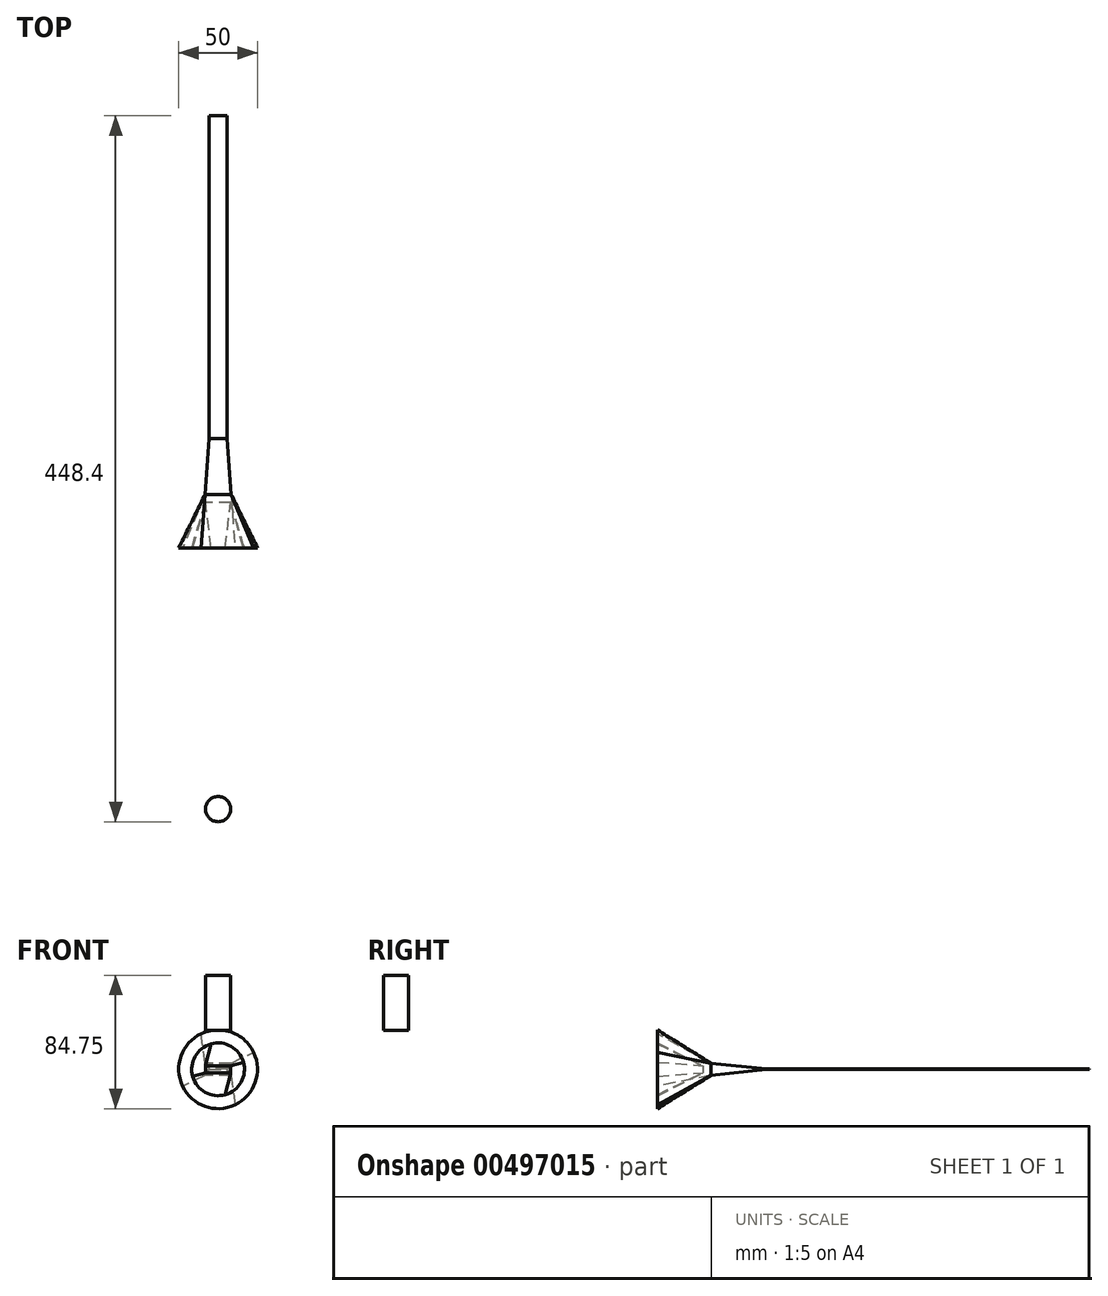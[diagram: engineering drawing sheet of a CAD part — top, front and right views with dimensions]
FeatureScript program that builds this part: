
annotation { "Feature Type Name" : "Feature", "Feature Type Description" : "" }
export const myFeature = defineFeature(function(context is Context, id is Id, definition is map)
    precondition{}
    {
        {
            var Q0;
            Q0=qCreatedBy(makeId("Front.planeOp"),FACE);
            var sketch = newSketch(context, id + "F0", { "sketchPlane" : qUnion([Q0])});
            skLineSegment(sketch, "E0.bottom", {"start": v(5.75, 0.16) * mm, "end": v(-5.75, 0.16) * mm});
            skLineSegment(sketch, "E0.top", {"start": v(5.75, -0.16) * mm, "end": v(-5.75, -0.16) * mm});
            skLineSegment(sketch, "E0.left", {"start": v(5.75, 0.16) * mm, "end": v(5.75, -0.16) * mm});
            skLineSegment(sketch, "E0.right", {"start": v(-5.75, 0.16) * mm, "end": v(-5.75, -0.16) * mm});
            skPoint(sketch, "E0.middle", {"position": v(0, 0) * mm});
            skSolve(sketch);
        }
        {
            var Q0;
            Q0 = qSketchRegion(id + "F0", true);
            extrude(context, id + "F1", {"entities" : qUnion([Q0]), "oppositeDirection" : true, "depth" : 205 * mm, "hasDraft" : true, "draftAngle" : 0 * degree});
        }
        {
            var Q0;
            Q0=qCreatedBy(makeId("Front.planeOp"),FACE);
            cPlane(context, id + "F2", {"entities" : qUnion([Q0]), "cplaneType" : CPlaneType.OFFSET, "offset" : 35.5 * mm, "width" : 150 * mm, "height" : 150 * mm});
        }
        {
            var Q0;
            Q0=qCreatedBy(id+"F2.planeOp",FACE);
            cPlane(context, id + "F3", {"entities" : qUnion([Q0]), "cplaneType" : CPlaneType.OFFSET, "offset" : 5 * mm, "width" : 150 * mm, "height" : 150 * mm});
        }
        {
            var Q0;
            Q0=qCreatedBy(id+"F3.planeOp",FACE);
            cPlane(context, id + "F4", {"entities" : qUnion([Q0]), "cplaneType" : CPlaneType.OFFSET, "offset" : 28.9 * mm, "width" : 150 * mm, "height" : 150 * mm});
        }
        {
            var Q0;
            Q0=qCreatedBy(id+"F4.planeOp",FACE);
            cPlane(context, id + "F5", {"entities" : qUnion([Q0]), "cplaneType" : CPlaneType.OFFSET, "offset" : 166 * mm, "width" : 150 * mm, "height" : 150 * mm});
        }
        {
            var Q0;
            Q0=qCreatedBy(id+"F2.planeOp",FACE);
            var sketch = newSketch(context, id + "F6", { "sketchPlane" : qUnion([Q0])});
            skLineSegment(sketch, "E1.bottom", {"start": v(8.25, 3.9) * mm, "end": v(-8.25, 3.9) * mm});
            skLineSegment(sketch, "E1.top", {"start": v(8.25, -3.9) * mm, "end": v(-8.25, -3.9) * mm});
            skLineSegment(sketch, "E1.left", {"start": v(8.25, -3.9) * mm, "end": v(8.25, 3.9) * mm});
            skLineSegment(sketch, "E1.right", {"start": v(-8.25, -3.9) * mm, "end": v(-8.25, 3.9) * mm});
            skSolve(sketch);
        }
        {
            var Q0;
            Q0=qCreatedBy(id+"F3.planeOp",FACE);
            var sketch = newSketch(context, id + "F7", { "sketchPlane" : qUnion([Q0])});
            skLineSegment(sketch, "E2.bottom", {"start": v(8, 2.25) * mm, "end": v(-8, 2.25) * mm});
            skLineSegment(sketch, "E2.top", {"start": v(8, -2.25) * mm, "end": v(-8, -2.25) * mm});
            skLineSegment(sketch, "E2.left", {"start": v(8, 2.25) * mm, "end": v(8, -2.25) * mm});
            skLineSegment(sketch, "E2.right", {"start": v(-8, 2.25) * mm, "end": v(-8, -2.25) * mm});
            skPoint(sketch, "E2.middle", {"position": v(0, 0) * mm});
            skSolve(sketch);
        }
        {
            var Q0;
            Q0=qCreatedBy(id+"F4.planeOp",FACE);
            var sketch = newSketch(context, id + "F8", { "sketchPlane" : qUnion([Q0])});
            skCircle(sketch, "E3", {"center": v(0, 0) * mm, "radius": 25 * mm});
            skSolve(sketch);
        }
        {
            var Q0;
            Q0=makeQuery(id+"F6.imprint","IMPRINT",FACE,{"disambiguationData":[TD([[makeQuery(id+"F6.imprint","IMPRINT",EDGE,{"derivedFrom":sQuery(id+"F6.wireOp",EDGE,"E1.bottom")}),1.0]])]});
            var Q1;
            Q1=makeQuery(id+"F1.opExtrude","CAP_FACE",FACE,{"disambiguationData":[OSD([sQuery(id+"F0.wireOp",EDGE,"E0.bottom"),sQuery(id+"F0.wireOp",EDGE,"E0.top"),sQuery(id+"F0.wireOp",EDGE,"E0.left"),sQuery(id+"F0.wireOp",EDGE,"E0.right")])],"isStart":true});
            loft(context, id + "F9", {"operationType" : NewBodyOperationType.ADD, "sheetProfilesArray" : [{ "sheetProfileEntities" : qUnion([Q0]) }, { "sheetProfileEntities" : qUnion([Q1]) }]});
        }
        {
            var Q1;
            Q1=makeQuery(id+"F9.opLoft","CAP_FACE",FACE,{"disambiguationData":[OSD([makeQuery(id+"F6.imprint","IMPRINT",FACE,{"disambiguationData":[TD([[makeQuery(id+"F6.imprint","IMPRINT",EDGE,{"derivedFrom":sQuery(id+"F6.wireOp",EDGE,"E1.bottom")}),1.0]])]})])],"isStart":true});
            var Q2;
            Q2=makeQuery(id+"F8.imprint","IMPRINT",FACE,{"disambiguationData":[TD([[makeQuery(id+"F8.imprint","IMPRINT",EDGE,{"derivedFrom":sQuery(id+"F8.wireOp",EDGE,"E3")}),1.0]])]});
            var Q3;
            Q3=makeQuery(id+"F9.opLoft","CAP_FACE",FACE,{"disambiguationData":[OSD([makeQuery(id+"F6.imprint","IMPRINT",FACE,{"disambiguationData":[TD([[makeQuery(id+"F6.imprint","IMPRINT",EDGE,{"derivedFrom":sQuery(id+"F6.wireOp",EDGE,"E1.bottom")}),1.0]])]})])],"isStart":true});
            var Q4;
            Q4=makeQuery(id+"F8.imprint","IMPRINT",FACE,{"disambiguationData":[TD([[makeQuery(id+"F8.imprint","IMPRINT",EDGE,{"derivedFrom":sQuery(id+"F8.wireOp",EDGE,"E3")}),1.0]])]});
            loft(context, id + "F10", {"operationType" : NewBodyOperationType.ADD, "sheetProfilesArray" : [{ "sheetProfileEntities" : qUnion([Q1]) }, { "sheetProfileEntities" : qUnion([Q2]) }], "wireProfilesArray" : [{ "wireProfileEntities" : qUnion([Q3]) }, { "wireProfileEntities" : qUnion([Q4]) }]});
        }
        {
            var Q0;
            Q0=makeQuery(id+"F10.opLoft","CAP_FACE",FACE,{"disambiguationData":[OSD([makeQuery(id+"F8.imprint","IMPRINT",FACE,{"disambiguationData":[TD([[makeQuery(id+"F8.imprint","IMPRINT",EDGE,{"derivedFrom":sQuery(id+"F8.wireOp",EDGE,"E3")}),1.0]])]})])],"isStart":true});
            var sketch = newSketch(context, id + "F11", { "sketchPlane" : qUnion([Q0])});
            skCircle(sketch, "E4", {"center": v(0, 0) * mm, "radius": 16.75 * mm});
            skSolve(sketch);
        }
        {
            var Q1;
            Q1=makeQuery(id+"F11.imprint","IMPRINT",FACE,{"disambiguationData":[TD([[makeQuery(id+"F11.imprint","IMPRINT",EDGE,{"derivedFrom":sQuery(id+"F11.wireOp",EDGE,"E4")}),1.0]])]});
            var Q2;
            Q2 = qSketchRegion(id + "F7", true);
            loft(context, id + "F12", {"operationType" : NewBodyOperationType.REMOVE, "sheetProfilesArray" : [{ "sheetProfileEntities" : qUnion([Q1]) }, { "sheetProfileEntities" : qUnion([Q2]) }]});
        }
        {
            var Q0;
            Q0=qCreatedBy(id+"F5.planeOp",FACE);
            var sketch = newSketch(context, id + "F13", { "sketchPlane" : qUnion([Q0])});
            skLineSegment(sketch, "E5.bottom", {"start": v(0, 59.75) * mm, "end": v(-8, 59.75) * mm});
            skLineSegment(sketch, "E5.top", {"start": v(0, 24.75) * mm, "end": v(-8, 24.75) * mm});
            skLineSegment(sketch, "E5.left", {"start": v(0, 59.75) * mm, "end": v(0, 24.75) * mm});
            skLineSegment(sketch, "E5.right", {"start": v(-8, 59.75) * mm, "end": v(-8, 24.75) * mm});
            skSolve(sketch);
        }
        {
            var Q0;
            Q0=makeQuery(id+"F13.imprint","IMPRINT",FACE,{"disambiguationData":[TD([[makeQuery(id+"F13.imprint","IMPRINT",EDGE,{"derivedFrom":sQuery(id+"F13.wireOp",EDGE,"E5.bottom")}),1.0]])]});
            var Q1;
            Q1=sQuery(id+"F13.wireOp",EDGE,"E5.left");
            revolve(context, id + "F14", {"entities" : qUnion([Q0]), "axis" : qUnion([Q1]), "revolveType" : RevolveType.FULL});
        }
        {
            var Q0;
            Q0 = qBodyType(qCreatedBy(id + "F11" ,EDGE), BodyType.WIRE);
            extrude(context, id + "F15", {"bodyType" : ToolBodyType.SURFACE, "surfaceEntities" : qUnion([Q0]), "depth" : 200 * mm, "offsetDistance" : 25 * mm});
        }
    });
